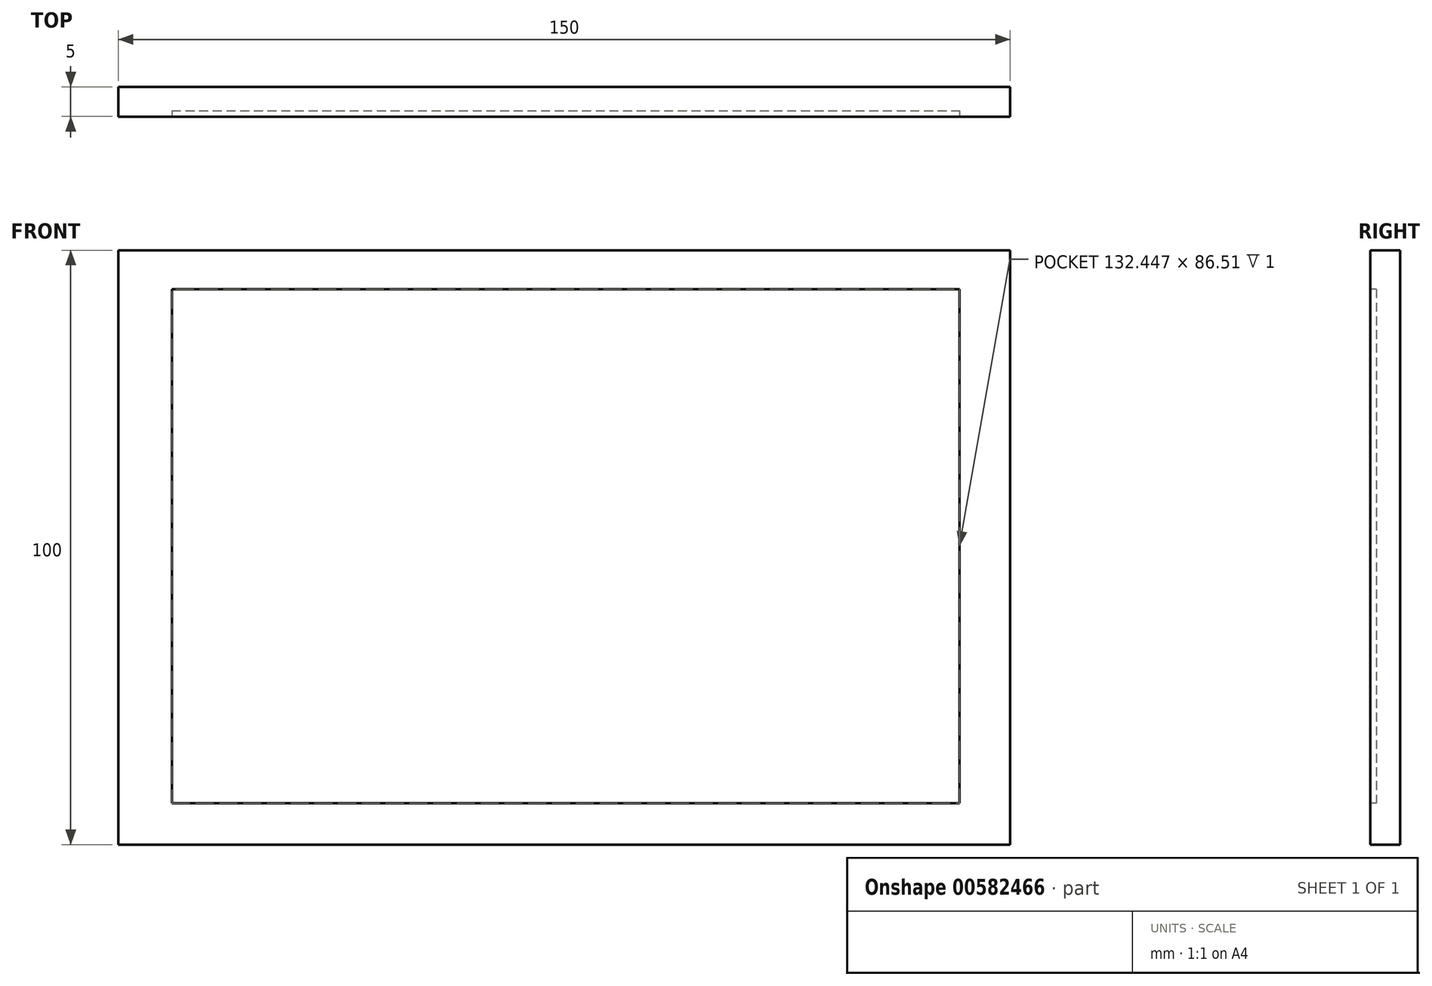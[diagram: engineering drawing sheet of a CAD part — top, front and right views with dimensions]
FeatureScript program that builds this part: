
annotation { "Feature Type Name" : "Feature", "Feature Type Description" : "" }
export const myFeature = defineFeature(function(context is Context, id is Id, definition is map)
    precondition{}
    {
        {
            var Q0;
            Q0=qCreatedBy(makeId("Top.planeOp"),FACE);
            var sketch = newSketch(context, id + "F0", { "sketchPlane" : qUnion([Q0])});
            skLineSegment(sketch, "E0.bottom", {"start": v(-57.34, 16.53) * mm, "end": v(92.66, 16.53) * mm});
            skLineSegment(sketch, "E0.top", {"start": v(-57.34, 21.53) * mm, "end": v(92.66, 21.53) * mm});
            skLineSegment(sketch, "E0.left", {"start": v(-57.34, 16.53) * mm, "end": v(-57.34, 21.53) * mm});
            skLineSegment(sketch, "E0.right", {"start": v(92.66, 16.53) * mm, "end": v(92.66, 21.53) * mm});
            skSolve(sketch);
        }
        {
            var Q0;
            Q0=makeQuery(id+"F0.imprint","IMPRINT",FACE,{"disambiguationData":[TD([[makeQuery(id+"F0.imprint","IMPRINT",EDGE,{"derivedFrom":sQuery(id+"F0.wireOp",EDGE,"E0.bottom")}),1.0]])]});
            extrude(context, id + "F1", {"entities" : qUnion([Q0]), "depth" : 100 * mm, "offsetDistance" : 25 * mm});
        }
        {
            var Q0;
            Q0=makeQuery(id+"F1.opExtrude","SWEPT_FACE",FACE,{"disambiguationData":[OSD([sQuery(id+"F0.wireOp",EDGE,"E0.bottom")])]});
            var sketch = newSketch(context, id + "F2", { "sketchPlane" : qUnion([Q0])});
            skLineSegment(sketch, "E1.bottom", {"start": v(-48.34, 93.48) * mm, "end": v(84.1, 93.48) * mm});
            skLineSegment(sketch, "E1.top", {"start": v(-48.34, 6.97) * mm, "end": v(84.1, 6.97) * mm});
            skLineSegment(sketch, "E1.left", {"start": v(-48.34, 93.48) * mm, "end": v(-48.34, 6.97) * mm});
            skLineSegment(sketch, "E1.right", {"start": v(84.1, 93.48) * mm, "end": v(84.1, 6.97) * mm});
            skSolve(sketch);
        }
        {
            var Q0;
            Q0=makeQuery(id+"F2.imprint","IMPRINT",FACE,{"disambiguationData":[TD([[makeQuery(id+"F2.imprint","IMPRINT",EDGE,{"derivedFrom":sQuery(id+"F2.wireOp",EDGE,"E1.bottom")}),-1.0]])]});
            extrude(context, id + "F3", {"entities" : qUnion([Q0]), "operationType" : NewBodyOperationType.REMOVE, "oppositeDirection" : true, "depth" : 1 * mm, "offsetDistance" : 25 * mm});
        }
    });
